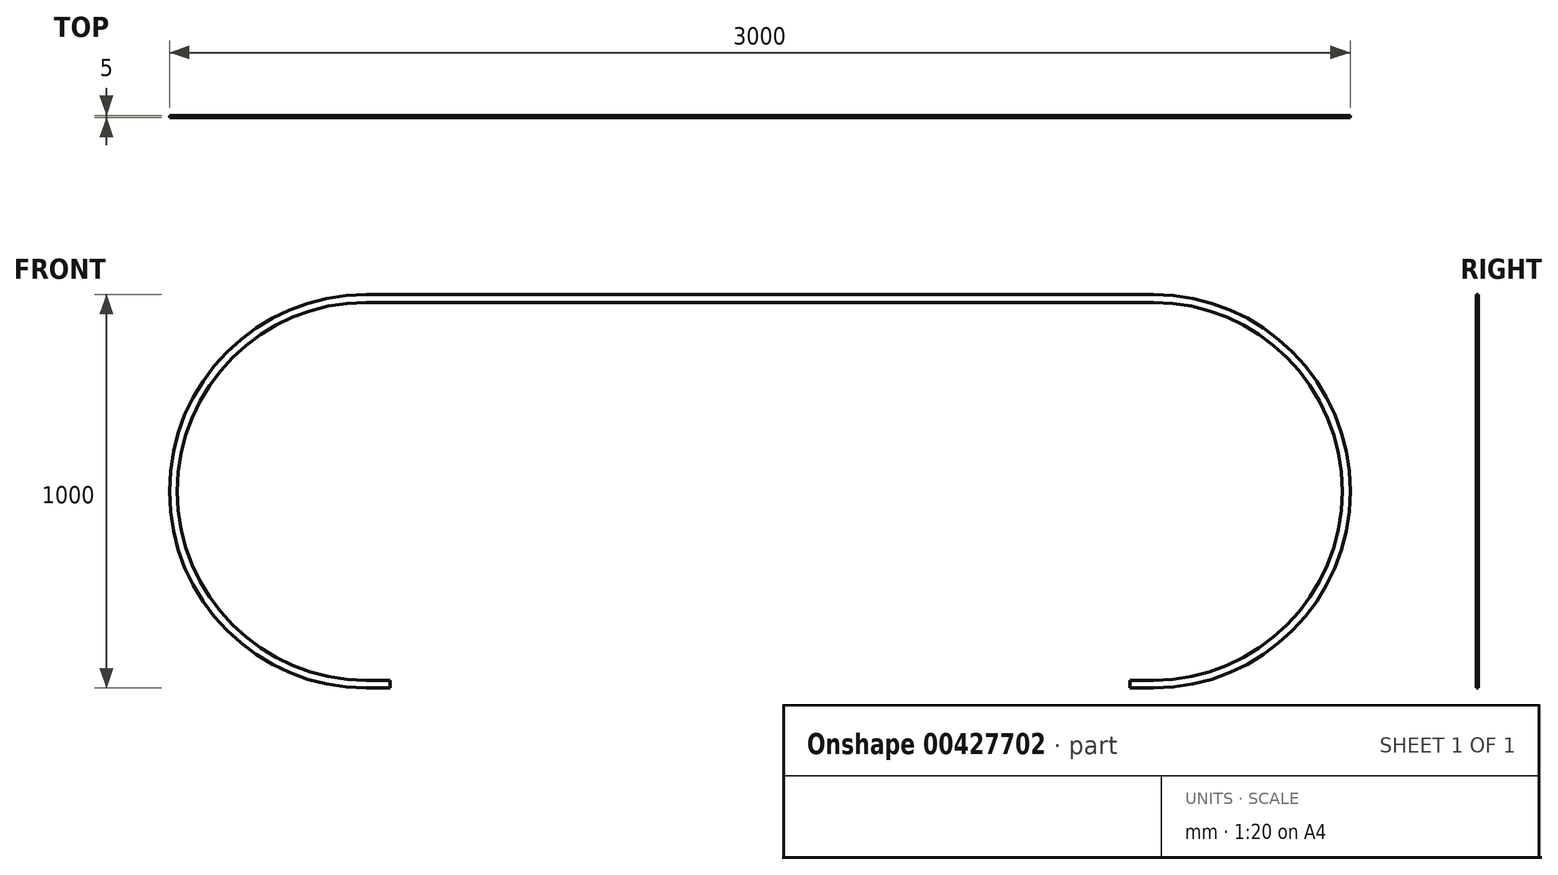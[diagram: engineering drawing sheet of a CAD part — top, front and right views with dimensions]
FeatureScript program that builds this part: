
annotation { "Feature Type Name" : "Feature", "Feature Type Description" : "" }
export const myFeature = defineFeature(function(context is Context, id is Id, definition is map)
    precondition{}
    {
        {
            var Q0;
            Q0=qCreatedBy(makeId("Front.planeOp"),FACE);
            var sketch = newSketch(context, id + "F0", { "sketchPlane" : qUnion([Q0])});
            skLineSegment(sketch, "E0.bottom", {"start": v(-1000, 10) * mm, "end": v(1000, 10) * mm});
            skLineSegment(sketch, "E0.top", {"start": v(-1000, -10) * mm, "end": v(1000, -10) * mm});
            skLineSegment(sketch, "E0.left", {"start": v(-1000, 10) * mm, "end": v(-1000, -10) * mm});
            skLineSegment(sketch, "E0.right", {"start": v(1000, 10) * mm, "end": v(1000, -10) * mm});
            skPoint(sketch, "E0.middle", {"position": v(0, 0) * mm});
            skArc(sketch, "E1", {"start": v(1000, -990) * mm, "mid": v(1500, -490) * mm, "end": v(1000, 10) * mm});
            skLineSegment(sketch, "E2", {"start": v(1000, -490) * mm, "end": v(1000, -10) * mm, "construction": true});
            skArc(sketch, "E3", {"start": v(1000, -970) * mm, "mid": v(1480, -490) * mm, "end": v(1000, -10) * mm});
            skArc(sketch, "E4", {"start": v(-1000, 10) * mm, "mid": v(-1500, -490) * mm, "end": v(-1000, -990) * mm});
            skArc(sketch, "E5", {"start": v(-1000, -10) * mm, "mid": v(-1480, -490) * mm, "end": v(-1000, -970) * mm});
            skLineSegment(sketch, "E6", {"start": v(-1000, -490) * mm, "end": v(-1000, -10) * mm, "construction": true});
            skLineSegment(sketch, "E7", {"start": v(-1000, -490) * mm, "end": v(-1000, -990) * mm, "construction": true});
            skLineSegment(sketch, "E8", {"start": v(-1000, -990) * mm, "end": v(-940, -990) * mm});
            skLineSegment(sketch, "E9", {"start": v(-940, -990) * mm, "end": v(-940, -970) * mm});
            skLineSegment(sketch, "E10", {"start": v(-940, -970) * mm, "end": v(-1000, -970) * mm});
            skLineSegment(sketch, "E11", {"start": v(1000, -490) * mm, "end": v(1000, -990) * mm});
            skLineSegment(sketch, "E12", {"start": v(1000, -990) * mm, "end": v(940, -990) * mm});
            skLineSegment(sketch, "E13", {"start": v(940, -990) * mm, "end": v(940, -970) * mm});
            skLineSegment(sketch, "E14", {"start": v(940, -970) * mm, "end": v(1000, -970) * mm});
            skSolve(sketch);
        }
        {
            var Q0;
            Q0 = qSketchRegion(id + "F0", true);
            extrude(context, id + "F1", {"entities" : qUnion([Q0]), "depth" : 5 * mm});
        }
    });
